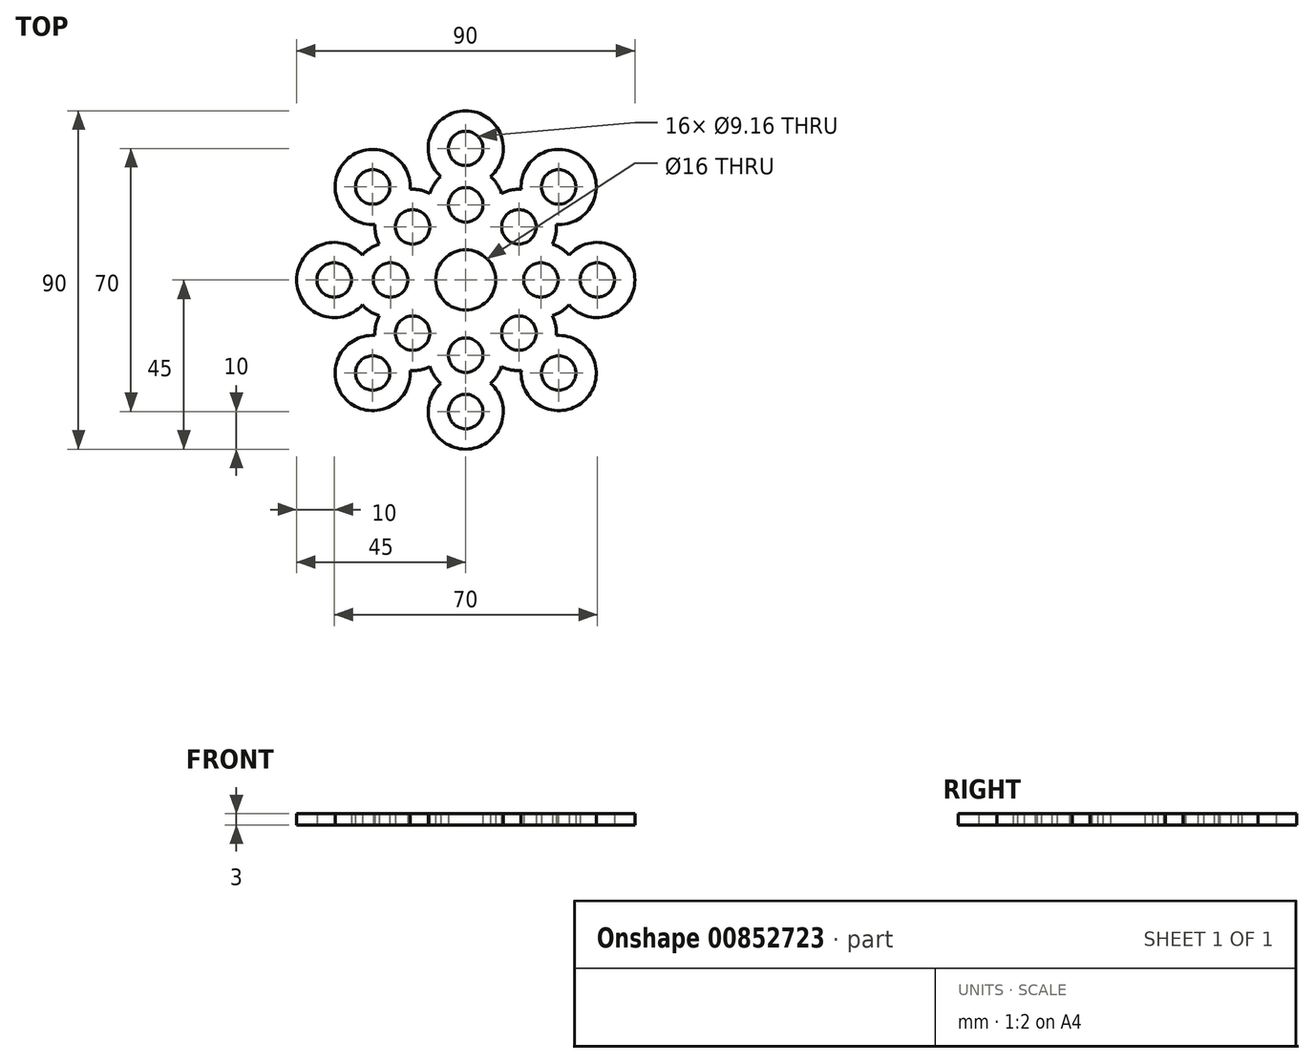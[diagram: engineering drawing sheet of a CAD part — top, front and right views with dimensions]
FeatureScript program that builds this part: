
annotation { "Feature Type Name" : "Feature", "Feature Type Description" : "" }
export const myFeature = defineFeature(function(context is Context, id is Id, definition is map)
    precondition{}
    {
        {
            var Q0;
            Q0=qCreatedBy(makeId("Top.planeOp"),FACE);
            var sketch = newSketch(context, id + "F0", { "sketchPlane" : qUnion([Q0])});
            skCircle(sketch, "E0", {"center": v(0, 0) * mm, "radius": 8 * mm});
            skCircle(sketch, "E1", {"center": v(0, 20) * mm, "radius": 4.58 * mm});
            skArc(sketch, "E2", {"start": v(-6.61, 27.5) * mm, "mid": v(-8.38, 25.46) * mm, "end": v(-9.53, 23.02) * mm});
            skCircle(sketch, "E3", {"center": v(0, 35) * mm, "radius": 4.58 * mm});
            skArc(sketch, "E4", {"start": v(6.61, 27.5) * mm, "mid": v(0, 45) * mm, "end": v(-6.61, 27.5) * mm});
            skArc(sketch, "E5.trimOffspring", {"start": v(9.53, 23.02) * mm, "mid": v(8.38, 25.46) * mm, "end": v(6.61, 27.5) * mm});
            skArc(sketch, "E6.1.0", {"start": v(-14.77, 24.12) * mm, "mid": v(-31.82, 31.82) * mm, "end": v(-24.12, 14.77) * mm});
            skCircle(sketch, "E6.1.1", {"center": v(-24.75, 24.75) * mm, "radius": 4.58 * mm});
            skCircle(sketch, "E6.1.2", {"center": v(-14.14, 14.14) * mm, "radius": 4.58 * mm});
            skArc(sketch, "E6.1.3", {"start": v(-9.53, 23.02) * mm, "mid": v(-12.08, 23.93) * mm, "end": v(-14.77, 24.12) * mm});
            skArc(sketch, "E6.1.4", {"start": v(-24.12, 14.77) * mm, "mid": v(-23.93, 12.08) * mm, "end": v(-23.02, 9.53) * mm});
            skArc(sketch, "E6.2.0", {"start": v(-27.5, 6.61) * mm, "mid": v(-45, 0) * mm, "end": v(-27.5, -6.61) * mm});
            skCircle(sketch, "E6.2.1", {"center": v(-35, 0) * mm, "radius": 4.58 * mm});
            skCircle(sketch, "E6.2.2", {"center": v(-20, 0) * mm, "radius": 4.58 * mm});
            skArc(sketch, "E6.2.3", {"start": v(-23.02, 9.53) * mm, "mid": v(-25.46, 8.38) * mm, "end": v(-27.5, 6.61) * mm});
            skArc(sketch, "E6.2.4", {"start": v(-27.5, -6.61) * mm, "mid": v(-25.46, -8.38) * mm, "end": v(-23.02, -9.53) * mm});
            skArc(sketch, "E6.3.0", {"start": v(-24.12, -14.77) * mm, "mid": v(-31.82, -31.82) * mm, "end": v(-14.77, -24.12) * mm});
            skCircle(sketch, "E6.3.1", {"center": v(-24.75, -24.75) * mm, "radius": 4.58 * mm});
            skCircle(sketch, "E6.3.2", {"center": v(-14.14, -14.14) * mm, "radius": 4.58 * mm});
            skArc(sketch, "E6.3.3", {"start": v(-23.02, -9.53) * mm, "mid": v(-23.93, -12.08) * mm, "end": v(-24.12, -14.77) * mm});
            skArc(sketch, "E6.3.4", {"start": v(-14.77, -24.12) * mm, "mid": v(-12.08, -23.93) * mm, "end": v(-9.53, -23.02) * mm});
            skArc(sketch, "E6.4.0", {"start": v(-6.61, -27.5) * mm, "mid": v(0, -45) * mm, "end": v(6.61, -27.5) * mm});
            skCircle(sketch, "E6.4.1", {"center": v(0, -35) * mm, "radius": 4.58 * mm});
            skCircle(sketch, "E6.4.2", {"center": v(0, -20) * mm, "radius": 4.58 * mm});
            skArc(sketch, "E6.4.3", {"start": v(-9.53, -23.02) * mm, "mid": v(-8.38, -25.46) * mm, "end": v(-6.61, -27.5) * mm});
            skArc(sketch, "E6.4.4", {"start": v(6.61, -27.5) * mm, "mid": v(8.38, -25.46) * mm, "end": v(9.53, -23.02) * mm});
            skArc(sketch, "E6.5.0", {"start": v(14.77, -24.12) * mm, "mid": v(31.82, -31.82) * mm, "end": v(24.12, -14.77) * mm});
            skCircle(sketch, "E6.5.1", {"center": v(24.75, -24.75) * mm, "radius": 4.58 * mm});
            skCircle(sketch, "E6.5.2", {"center": v(14.14, -14.14) * mm, "radius": 4.58 * mm});
            skArc(sketch, "E6.5.3", {"start": v(9.53, -23.02) * mm, "mid": v(12.08, -23.93) * mm, "end": v(14.77, -24.12) * mm});
            skArc(sketch, "E6.5.4", {"start": v(24.12, -14.77) * mm, "mid": v(23.93, -12.08) * mm, "end": v(23.02, -9.53) * mm});
            skArc(sketch, "E6.6.0", {"start": v(27.5, -6.61) * mm, "mid": v(45, 0) * mm, "end": v(27.5, 6.61) * mm});
            skCircle(sketch, "E6.6.1", {"center": v(35, 0) * mm, "radius": 4.58 * mm});
            skCircle(sketch, "E6.6.2", {"center": v(20, 0) * mm, "radius": 4.58 * mm});
            skArc(sketch, "E6.6.3", {"start": v(23.02, -9.53) * mm, "mid": v(25.46, -8.38) * mm, "end": v(27.5, -6.61) * mm});
            skArc(sketch, "E6.6.4", {"start": v(27.5, 6.61) * mm, "mid": v(25.46, 8.38) * mm, "end": v(23.02, 9.53) * mm});
            skArc(sketch, "E6.7.0", {"start": v(24.12, 14.77) * mm, "mid": v(31.82, 31.82) * mm, "end": v(14.77, 24.12) * mm});
            skCircle(sketch, "E6.7.1", {"center": v(24.75, 24.75) * mm, "radius": 4.58 * mm});
            skCircle(sketch, "E6.7.2", {"center": v(14.14, 14.14) * mm, "radius": 4.58 * mm});
            skArc(sketch, "E6.7.3", {"start": v(23.02, 9.53) * mm, "mid": v(23.93, 12.08) * mm, "end": v(24.12, 14.77) * mm});
            skArc(sketch, "E6.7.4", {"start": v(14.77, 24.12) * mm, "mid": v(12.08, 23.93) * mm, "end": v(9.53, 23.02) * mm});
            skSolve(sketch);
        }
        {
            var Q0;
            Q0 = qSketchRegion(id + "F0", true);
            extrude(context, id + "F1", {"entities" : qUnion([Q0]), "depth" : 3 * mm, "offsetDistance" : 25 * mm});
        }
    });
